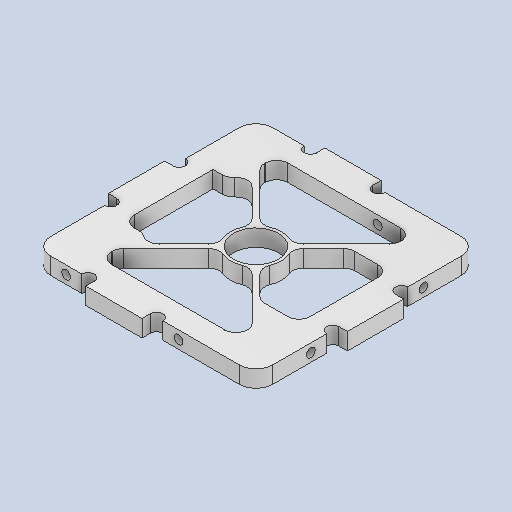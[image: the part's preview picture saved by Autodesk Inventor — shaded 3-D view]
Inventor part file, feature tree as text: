
AUTODESK INVENTOR PART (.ipt)
format: ipt  version: 2025.1 (Build 291241000, 241)  size: 372,736 bytes
history: native  units: mm
features: sketch x6, hole x4, extrude x2, fillet x2, projected_geometry x1
ambient origin geometry x8: Origin, YZ Plane, XZ Plane, XY Plane, X Axis, Y Axis, Z Axis, Center Point
bodies: Body1 (feature_tree)
feature tree (15):
  extrude  "押し出し2"  Depth=39.5mm
  hole  "穴1"  [1 undecoded]
  hole  "穴2"  [1 undecoded]
  hole  "穴3"  [1 undecoded]
  hole  "穴4"  [1 undecoded]
  extrude  "押し出し3"  Depth=10.0mm
  fillet  "フィレット1"  Radius=2.2mm
  fillet  "フィレット2"  [1 undecoded]
  sketch  "スケッチ1"
  sketch  "スケッチ2"
  sketch  "スケッチ3"
  projected_geometry  "投影ループ1"
  sketch  "スケッチ4"
  sketch  "スケッチ5"
  sketch  "スケッチ6"
note: 5 required parameter values undecoded (feature->parameter linkage not recoverable at this tier; creation-order binding heuristic only, values carry confidence <= 0.55)
